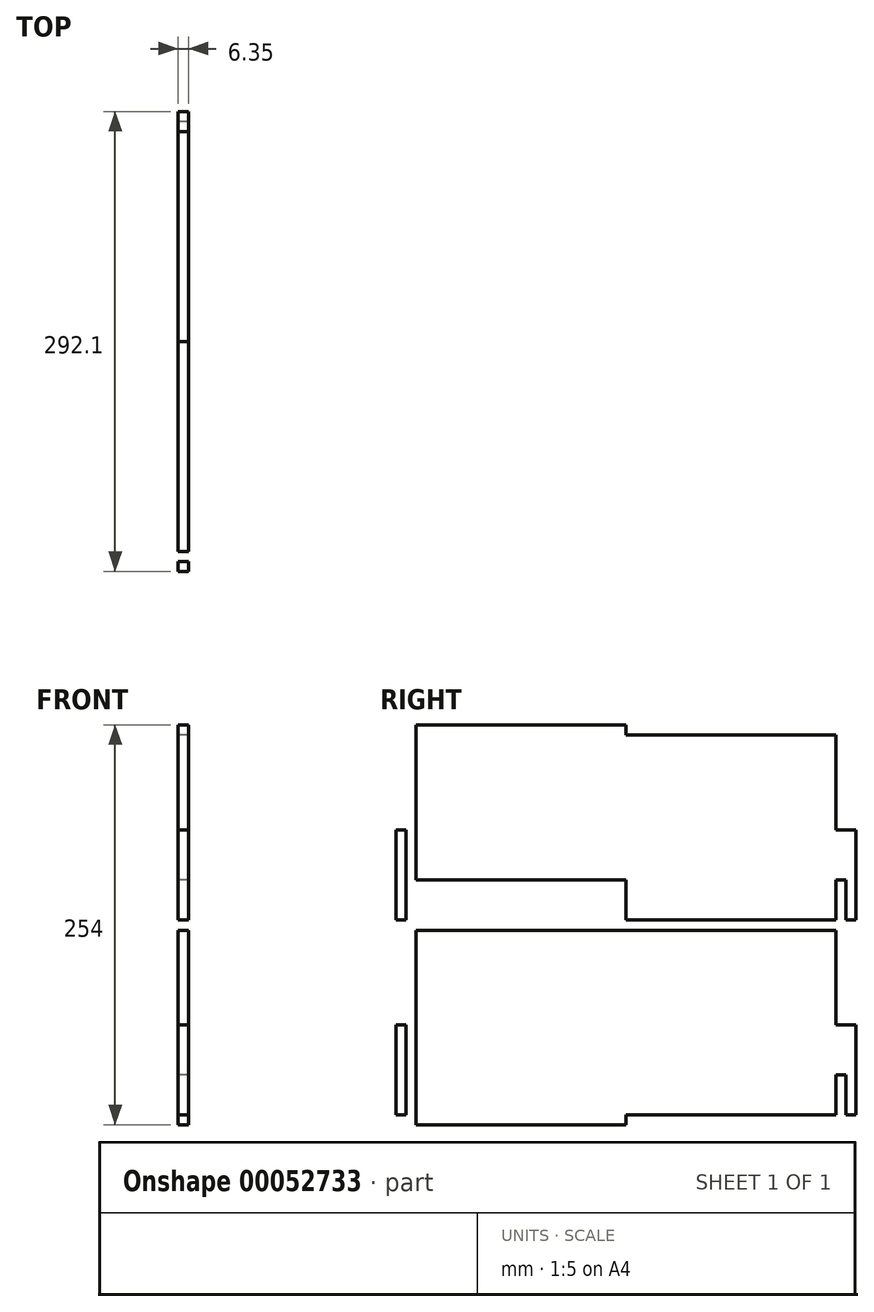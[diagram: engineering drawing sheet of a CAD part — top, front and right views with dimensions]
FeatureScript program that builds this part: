
annotation { "Feature Type Name" : "Feature", "Feature Type Description" : "" }
export const myFeature = defineFeature(function(context is Context, id is Id, definition is map)
    precondition{}
    {
        {
            var Q0;
            Q0=qCreatedBy(makeId("Right.planeOp"),FACE);
            var sketch = newSketch(context, id + "F0", { "sketchPlane" : qUnion([Q0])});
            skLineSegment(sketch, "E0.rect.bottom", {"start": v(-133.35, 120.65) * mm, "end": v(133.35, 120.65) * mm});
            skLineSegment(sketch, "E0.rect.top", {"start": v(-133.35, -120.65) * mm, "end": v(133.35, -120.65) * mm});
            skLineSegment(sketch, "E0.rect.left", {"start": v(-133.35, 120.65) * mm, "end": v(-133.35, -120.65) * mm});
            skLineSegment(sketch, "E0.rect.right", {"start": v(133.35, 120.65) * mm, "end": v(133.35, -120.65) * mm});
            skPoint(sketch, "E0.rect.middle", {"position": v(0, 0) * mm});
            skPoint(sketch, "E1.firstSnap0", {"position": v(0, 120.65) * mm});
            skLineSegment(sketch, "E1.left", {"start": v(0, 127) * mm, "end": v(0, -127) * mm});
            skLineSegment(sketch, "E2", {"start": v(0, -3.66) * mm, "end": v(133.35, -3.66) * mm});
            skLineSegment(sketch, "E3", {"start": v(0, 3.18) * mm, "end": v(133.35, 3.18) * mm});
            skLineSegment(sketch, "E4", {"start": v(0, 127) * mm, "end": v(-133.35, 127) * mm});
            skLineSegment(sketch, "E5", {"start": v(0, -127) * mm, "end": v(-133.35, -127) * mm});
            skLineSegment(sketch, "E6", {"start": v(-133.35, 127) * mm, "end": v(-133.35, -127) * mm});
            skLineSegment(sketch, "E7", {"start": v(146.05, 3.18) * mm, "end": v(133.35, 3.18) * mm});
            skLineSegment(sketch, "E8", {"start": v(146.05, 3.18) * mm, "end": v(146.05, 60.33) * mm});
            skLineSegment(sketch, "E9", {"start": v(146.05, 60.33) * mm, "end": v(139.7, 60.33) * mm});
            skPoint(sketch, "E9.endSnap0", {"position": v(139.7, 3.18) * mm});
            skLineSegment(sketch, "E10", {"start": v(139.7, 60.33) * mm, "end": v(139.7, 28.58) * mm});
            skLineSegment(sketch, "E11", {"start": v(139.7, 28.58) * mm, "end": v(133.35, 28.58) * mm});
            skLineSegment(sketch, "E12", {"start": v(133.35, -120.65) * mm, "end": v(146.05, -120.65) * mm});
            skLineSegment(sketch, "E13", {"start": v(146.05, -120.65) * mm, "end": v(146.05, -63.5) * mm});
            skLineSegment(sketch, "E14", {"start": v(146.05, -63.5) * mm, "end": v(139.7, -63.5) * mm});
            skLineSegment(sketch, "E15", {"start": v(139.7, -63.5) * mm, "end": v(139.7, -95.25) * mm});
            skLineSegment(sketch, "E16", {"start": v(139.7, -95.25) * mm, "end": v(133.35, -95.25) * mm});
            skLineSegment(sketch, "E17", {"start": v(133.35, -3.66) * mm, "end": v(133.35, -3.66) * mm});
            skLineSegment(sketch, "E18", {"start": v(139.7, 28.58) * mm, "end": v(139.7, 3.18) * mm});
            skLineSegment(sketch, "E19", {"start": v(139.7, -95.25) * mm, "end": v(139.7, -120.65) * mm});
            skLineSegment(sketch, "E20", {"start": v(139.7, -63.5) * mm, "end": v(133.35, -63.5) * mm});
            skLineSegment(sketch, "E21", {"start": v(139.7, 60.33) * mm, "end": v(133.35, 60.33) * mm});
            skLineSegment(sketch, "E22", {"start": v(146.05, 60.33) * mm, "end": v(-146.05, 60.32) * mm});
            skLineSegment(sketch, "E23", {"start": v(139.7, -95.25) * mm, "end": v(-146.05, -95.25) * mm});
            skLineSegment(sketch, "E24", {"start": v(139.7, 28.58) * mm, "end": v(-146.05, 28.58) * mm});
            skLineSegment(sketch, "E25", {"start": v(-146.05, 60.32) * mm, "end": v(-146.05, -120.65) * mm});
            skLineSegment(sketch, "E26", {"start": v(146.05, -63.5) * mm, "end": v(-146.05, -63.5) * mm});
            skLineSegment(sketch, "E27", {"start": v(-133.35, -120.65) * mm, "end": v(-146.05, -120.65) * mm});
            skLineSegment(sketch, "E28", {"start": v(-139.7, -120.65) * mm, "end": v(-139.7, 60.32) * mm});
            skLineSegment(sketch, "E29", {"start": v(0, 3.18) * mm, "end": v(-146.05, 3.18) * mm});
            skLineSegment(sketch, "E30.top", {"start": v(-133.35, -127) * mm, "end": v(-146.05, -127) * mm});
            skLineSegment(sketch, "E30.left", {"start": v(-133.35, -120.65) * mm, "end": v(-133.35, -127) * mm});
            skLineSegment(sketch, "E30.right", {"start": v(-146.05, -120.65) * mm, "end": v(-146.05, -127) * mm});
            skLineSegment(sketch, "E31", {"start": v(0, -3.66) * mm, "end": v(-146.05, -3.66) * mm});
            skSolve(sketch);
        }
        {
            var Q0;
            {var subQ5=sQuery(id+"F0.wireOp",EDGE,"9bf9b08d-dc9f-4cfe-882b-b09e2634e2f8");Q0=makeQuery(id+"F0.imprint","IMPRINT",FACE,{"disambiguationData":[TD([[makeQuery(id+"F0.imprint","IMPRINT",EDGE,{"derivedFrom":subQ5}),1.0]])]});}
            var Q1;
            {var subQ3=sQuery(id+"F0.wireOp",EDGE,"E0.rect.bottom");var subQ5=sQuery(id+"F0.wireOp",EDGE,"E1.right");var subQ9=makeQuery(id+"F0.imprint","INTERSECT",VERTEX,{"derivedFrom":[subQ3,subQ5]});Q1=makeQuery(id+"F0.imprint","IMPRINT",FACE,{"disambiguationData":[TD([[makeQuery(id+"F0.imprint","IMPRINT",EDGE,{"disambiguationData":[TD([[subQ9,1.0]])],"derivedFrom":subQ3}),-1.0]])]});}
            var Q2;
            {var subQ5=sQuery(id+"F0.wireOp",EDGE,"E1.bottom");Q2=makeQuery(id+"F0.imprint","IMPRINT",FACE,{"disambiguationData":[TD([[makeQuery(id+"F0.imprint","IMPRINT",EDGE,{"derivedFrom":subQ5}),-1.0]])]});}
            var Q3;
            {var subQ5=sQuery(id+"F0.wireOp",EDGE,"E1.top");Q3=makeQuery(id+"F0.imprint","IMPRINT",FACE,{"disambiguationData":[TD([[makeQuery(id+"F0.imprint","IMPRINT",EDGE,{"derivedFrom":subQ5}),1.0]])]});}
            var Q4;
            {var subQ5=sQuery(id+"F0.wireOp",EDGE,"234cc6d3-e0ab-4cdc-a50d-860a52f913cc");Q4=makeQuery(id+"F0.imprint","IMPRINT",FACE,{"disambiguationData":[TD([[makeQuery(id+"F0.imprint","IMPRINT",EDGE,{"derivedFrom":subQ5}),1.0]])]});}
            var Q5;
            {var subQ5=sQuery(id+"F0.wireOp",EDGE,"E2");Q5=makeQuery(id+"F0.imprint","IMPRINT",FACE,{"disambiguationData":[TD([[makeQuery(id+"F0.imprint","IMPRINT",EDGE,{"derivedFrom":subQ5}),-1.0]])]});}
            var Q6;
            {var subQ3=sQuery(id+"F0.wireOp",EDGE,"E6");var subQ7=sQuery(id+"F0.wireOp",EDGE,"E0.rect.bottom");var subQ9=makeQuery(id+"F0.imprint","INTERSECT",VERTEX,{"derivedFrom":[subQ7,subQ3]});Q6=makeQuery(id+"F0.imprint","IMPRINT",FACE,{"disambiguationData":[TD([[makeQuery(id+"F0.imprint","IMPRINT",EDGE,{"disambiguationData":[TD([[subQ9,-1.0]])],"derivedFrom":subQ7}),-1.0]])]});}
            var Q7;
            {var subQ5=sQuery(id+"F0.wireOp",EDGE,"E4");Q7=makeQuery(id+"F0.imprint","IMPRINT",FACE,{"disambiguationData":[TD([[makeQuery(id+"F0.imprint","IMPRINT",EDGE,{"derivedFrom":subQ5}),1.0]])]});}
            var Q8;
            {var subQ5=sQuery(id+"F0.wireOp",EDGE,"E5");Q8=makeQuery(id+"F0.imprint","IMPRINT",FACE,{"disambiguationData":[TD([[makeQuery(id+"F0.imprint","IMPRINT",EDGE,{"derivedFrom":subQ5}),-1.0]])]});}
            var Q9;
            {var subQ4=sQuery(id+"F0.wireOp",EDGE,"E3");Q9=makeQuery(id+"F0.imprint","IMPRINT",FACE,{"disambiguationData":[TD([[makeQuery(id+"F0.imprint","IMPRINT",EDGE,{"derivedFrom":subQ4}),1.0]])]});}
            var Q10;
            Q10=makeQuery(id+"F0.imprint","IMPRINT",FACE,{"disambiguationData":[TD([[makeQuery(id+"F0.imprint","IMPRINT",EDGE,{"derivedFrom":sQuery(id+"F0.wireOp",EDGE,"E10")}),-1.0]])]});
            var Q11;
            {var subQ0=sQuery(id+"F0.wireOp",EDGE,"E8");Q11=makeQuery(id+"F0.imprint","IMPRINT",FACE,{"disambiguationData":[TD([[makeQuery(id+"F0.imprint","IMPRINT",EDGE,{"derivedFrom":subQ0}),1.0]])]});}
            var Q12;
            {var subQ0=sQuery(id+"F0.wireOp",EDGE,"E13");Q12=makeQuery(id+"F0.imprint","IMPRINT",FACE,{"disambiguationData":[TD([[makeQuery(id+"F0.imprint","IMPRINT",EDGE,{"derivedFrom":subQ0}),1.0]])]});}
            var Q13;
            Q13=makeQuery(id+"F0.imprint","IMPRINT",FACE,{"disambiguationData":[TD([[makeQuery(id+"F0.imprint","IMPRINT",EDGE,{"derivedFrom":sQuery(id+"F0.wireOp",EDGE,"E15")}),-1.0]])]});
            var Q14;
            {var subQ0=sQuery(id+"F0.wireOp",EDGE,"E22");var subQ1=sQuery(id+"F0.wireOp",EDGE,"E0.rect.right");var subQ2=makeQuery(id+"F0.imprint","INTERSECT",VERTEX,{"derivedFrom":[subQ1,subQ0]});Q14=makeQuery(id+"F0.imprint","IMPRINT",FACE,{"disambiguationData":[TD([[makeQuery(id+"F0.imprint","IMPRINT",EDGE,{"disambiguationData":[TD([[subQ2,-1.0]])],"derivedFrom":subQ1}),-1.0]])]});}
            var Q15;
            {var subQ0=sQuery(id+"F0.wireOp",EDGE,"E22");var subQ1=sQuery(id+"F0.wireOp",EDGE,"E1.left");var subQ2=makeQuery(id+"F0.imprint","INTERSECT",VERTEX,{"derivedFrom":[subQ1,subQ0]});Q15=makeQuery(id+"F0.imprint","IMPRINT",FACE,{"disambiguationData":[TD([[makeQuery(id+"F0.imprint","IMPRINT",EDGE,{"disambiguationData":[TD([[subQ2,-1.0]])],"derivedFrom":subQ1}),-1.0]])]});}
            var Q16;
            {var subQ1=sQuery(id+"F0.wireOp",EDGE,"E1.left");var subQ5=makeQuery(id+"F0.imprint","INTERSECT",VERTEX,{"derivedFrom":[subQ1,sQuery(id+"F0.wireOp",EDGE,"E2")]});Q16=makeQuery(id+"F0.imprint","IMPRINT",FACE,{"disambiguationData":[TD([[makeQuery(id+"F0.imprint","IMPRINT",EDGE,{"disambiguationData":[TD([[subQ5,-1.0]])],"derivedFrom":subQ1}),-1.0]])]});}
            var Q17;
            {var subQ3=sQuery(id+"F0.wireOp",EDGE,"E24");var subQ5=sQuery(id+"F0.wireOp",EDGE,"E6");var subQ6=makeQuery(id+"F0.imprint","INTERSECT",VERTEX,{"derivedFrom":[subQ5,subQ3]});Q17=makeQuery(id+"F0.imprint","IMPRINT",FACE,{"disambiguationData":[TD([[makeQuery(id+"F0.imprint","IMPRINT",EDGE,{"disambiguationData":[TD([[subQ6,-1.0]])],"derivedFrom":subQ5}),1.0]])]});}
            var Q18;
            {var subQ0=sQuery(id+"F0.wireOp",EDGE,"E26");var subQ1=sQuery(id+"F0.wireOp",EDGE,"E1.left");var subQ2=makeQuery(id+"F0.imprint","INTERSECT",VERTEX,{"derivedFrom":[subQ1,subQ0]});Q18=makeQuery(id+"F0.imprint","IMPRINT",FACE,{"disambiguationData":[TD([[makeQuery(id+"F0.imprint","IMPRINT",EDGE,{"disambiguationData":[TD([[subQ2,-1.0]])],"derivedFrom":subQ1}),-1.0]])]});}
            var Q19;
            {var subQ0=sQuery(id+"F0.wireOp",EDGE,"E26");var subQ1=sQuery(id+"F0.wireOp",EDGE,"E0.rect.right");var subQ2=makeQuery(id+"F0.imprint","INTERSECT",VERTEX,{"derivedFrom":[subQ1,subQ0]});Q19=makeQuery(id+"F0.imprint","IMPRINT",FACE,{"disambiguationData":[TD([[makeQuery(id+"F0.imprint","IMPRINT",EDGE,{"disambiguationData":[TD([[subQ2,-1.0]])],"derivedFrom":subQ1}),-1.0]])]});}
            var Q20;
            {var subQ1=sQuery(id+"F0.wireOp",EDGE,"E0.rect.top");var subQ3=sQuery(id+"F0.wireOp",EDGE,"E1.left");var subQ4=makeQuery(id+"F0.imprint","INTERSECT",VERTEX,{"derivedFrom":[subQ1,subQ3]});Q20=makeQuery(id+"F0.imprint","IMPRINT",FACE,{"disambiguationData":[TD([[makeQuery(id+"F0.imprint","IMPRINT",EDGE,{"disambiguationData":[TD([[subQ4,1.0]])],"derivedFrom":subQ3}),1.0]])]});}
            var Q21;
            {var subQ1=sQuery(id+"F0.wireOp",EDGE,"E0.rect.top");var subQ3=sQuery(id+"F0.wireOp",EDGE,"E1.left");var subQ4=makeQuery(id+"F0.imprint","INTERSECT",VERTEX,{"derivedFrom":[subQ1,subQ3]});Q21=makeQuery(id+"F0.imprint","IMPRINT",FACE,{"disambiguationData":[TD([[makeQuery(id+"F0.imprint","IMPRINT",EDGE,{"disambiguationData":[TD([[subQ4,1.0]])],"derivedFrom":subQ3}),-1.0]])]});}
            var Q22;
            {var subQ0=sQuery(id+"F0.wireOp",EDGE,"E25");var subQ1=sQuery(id+"F0.wireOp",EDGE,"E23");var subQ2=makeQuery(id+"F0.imprint","INTERSECT",VERTEX,{"derivedFrom":[subQ1,subQ0]});Q22=makeQuery(id+"F0.imprint","IMPRINT",FACE,{"disambiguationData":[TD([[makeQuery(id+"F0.imprint","IMPRINT",EDGE,{"disambiguationData":[TD([[subQ2,1.0]])],"derivedFrom":subQ1}),-1.0]])]});}
            var Q23;
            {var subQ0=sQuery(id+"F0.wireOp",EDGE,"E25");var subQ1=sQuery(id+"F0.wireOp",EDGE,"E23");var subQ2=makeQuery(id+"F0.imprint","INTERSECT",VERTEX,{"derivedFrom":[subQ1,subQ0]});Q23=makeQuery(id+"F0.imprint","IMPRINT",FACE,{"disambiguationData":[TD([[makeQuery(id+"F0.imprint","IMPRINT",EDGE,{"disambiguationData":[TD([[subQ2,1.0]])],"derivedFrom":subQ1}),1.0]])]});}
            var Q24;
            {var subQ0=sQuery(id+"F0.wireOp",EDGE,"E25");var subQ1=sQuery(id+"F0.wireOp",EDGE,"E24");var subQ2=makeQuery(id+"F0.imprint","INTERSECT",VERTEX,{"derivedFrom":[subQ1,subQ0]});Q24=makeQuery(id+"F0.imprint","IMPRINT",FACE,{"disambiguationData":[TD([[makeQuery(id+"F0.imprint","IMPRINT",EDGE,{"disambiguationData":[TD([[subQ2,1.0]])],"derivedFrom":subQ1}),1.0]])]});}
            var Q25;
            {var subQ0=sQuery(id+"F0.wireOp",EDGE,"E25");var subQ1=sQuery(id+"F0.wireOp",EDGE,"E22");var subQ2=makeQuery(id+"F0.imprint","INTERSECT",VERTEX,{"derivedFrom":[subQ1,subQ0]});Q25=makeQuery(id+"F0.imprint","IMPRINT",FACE,{"disambiguationData":[TD([[makeQuery(id+"F0.imprint","IMPRINT",EDGE,{"disambiguationData":[TD([[subQ2,1.0]])],"derivedFrom":subQ1}),1.0]])]});}
            var Q26;
            {var subQ3=sQuery(id+"F0.wireOp",EDGE,"E29");var subQ5=sQuery(id+"F0.wireOp",EDGE,"E6");var subQ6=makeQuery(id+"F0.imprint","INTERSECT",VERTEX,{"derivedFrom":[subQ5,subQ3]});Q26=makeQuery(id+"F0.imprint","IMPRINT",FACE,{"disambiguationData":[TD([[makeQuery(id+"F0.imprint","IMPRINT",EDGE,{"disambiguationData":[TD([[subQ6,-1.0]])],"derivedFrom":subQ5}),1.0]])]});}
            var Q27;
            {var subQ0=sQuery(id+"F0.wireOp",EDGE,"E22");var subQ1=sQuery(id+"F0.wireOp",EDGE,"E6");var subQ2=makeQuery(id+"F0.imprint","INTERSECT",VERTEX,{"derivedFrom":[subQ1,subQ0]});Q27=makeQuery(id+"F0.imprint","IMPRINT",FACE,{"disambiguationData":[TD([[makeQuery(id+"F0.imprint","IMPRINT",EDGE,{"disambiguationData":[TD([[subQ2,-1.0]])],"derivedFrom":subQ1}),-1.0]])]});}
            var Q28;
            {var subQ0=sQuery(id+"F0.wireOp",EDGE,"E26");var subQ1=sQuery(id+"F0.wireOp",EDGE,"E6");var subQ2=makeQuery(id+"F0.imprint","INTERSECT",VERTEX,{"derivedFrom":[subQ1,subQ0]});Q28=makeQuery(id+"F0.imprint","IMPRINT",FACE,{"disambiguationData":[TD([[makeQuery(id+"F0.imprint","IMPRINT",EDGE,{"disambiguationData":[TD([[subQ2,-1.0]])],"derivedFrom":subQ1}),-1.0]])]});}
            extrude(context, id + "F1", {"entities" : qUnion([Q0, Q1, Q2, Q3, Q4, Q5, Q6, Q7, Q8, Q9, Q10, Q11, Q12, Q13, Q14, Q15, Q16, Q17, Q18, Q19, Q20, Q21, Q22, Q23, Q24, Q25, Q26, Q27, Q28]), "depth" : 6.35 * mm});
        }
    });
